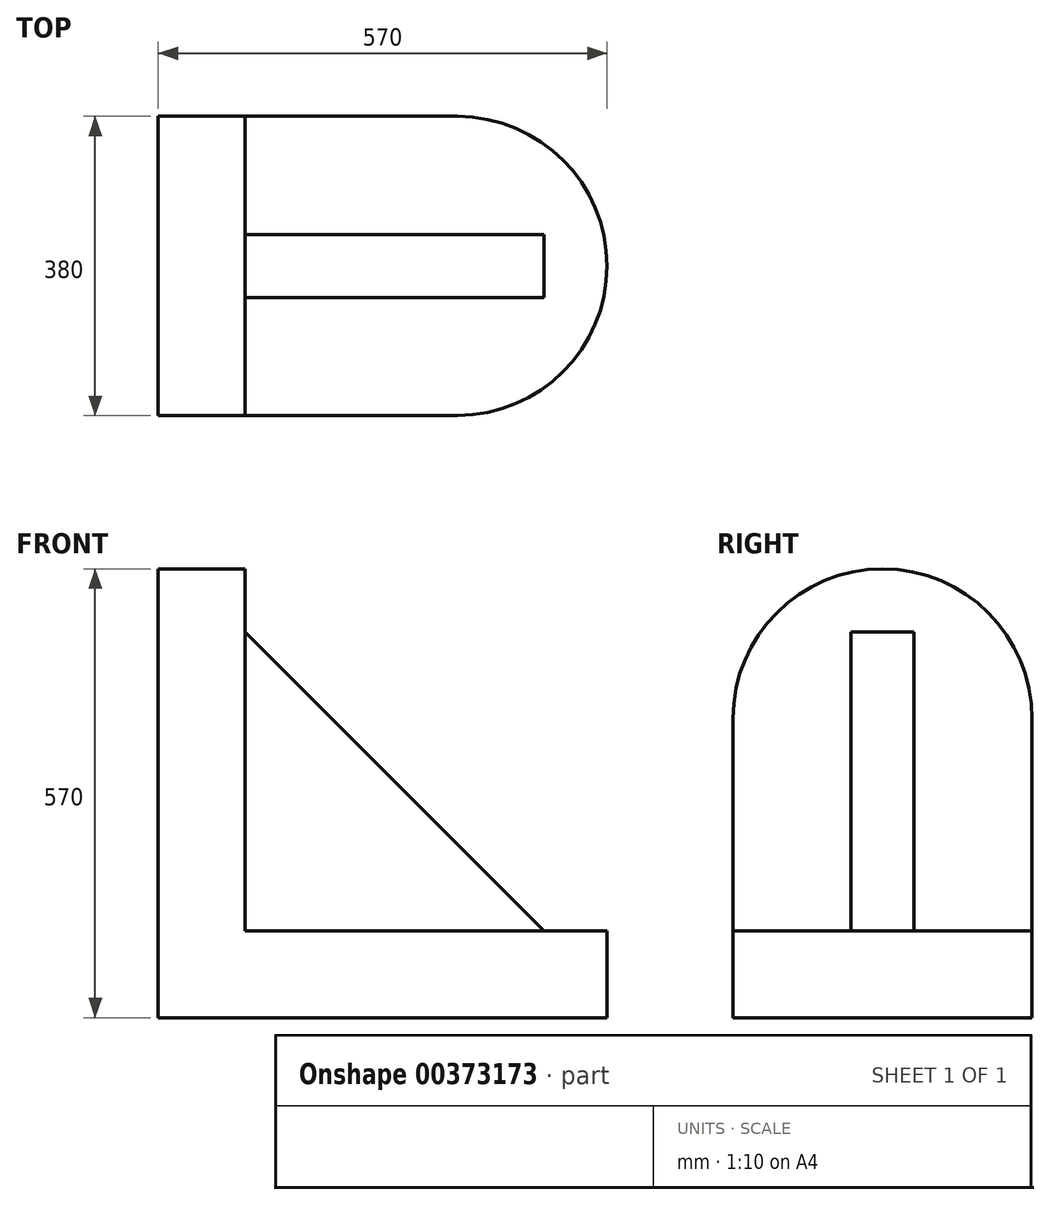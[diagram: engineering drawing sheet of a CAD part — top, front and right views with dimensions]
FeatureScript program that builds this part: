
annotation { "Feature Type Name" : "Feature", "Feature Type Description" : "" }
export const myFeature = defineFeature(function(context is Context, id is Id, definition is map)
    precondition{}
    {
        {
            var Q0;
            Q0=qCreatedBy(makeId("Top.planeOp"),FACE);
            var sketch = newSketch(context, id + "F0", { "sketchPlane" : qUnion([Q0])});
            skLineSegment(sketch, "E0.bottom", {"start": v(0, 0) * mm, "end": v(380, 0) * mm});
            skLineSegment(sketch, "E0.top", {"start": v(0, 380) * mm, "end": v(380, 380) * mm});
            skLineSegment(sketch, "E0.left", {"start": v(0, 0) * mm, "end": v(0, 380) * mm});
            skArc(sketch, "E1", {"start": v(380, 0) * mm, "mid": v(570, 190) * mm, "end": v(380, 380) * mm});
            skSolve(sketch);
        }
        {
            var Q0;
            Q0 = qSketchRegion(id + "F0", true);
            extrude(context, id + "F1", {"entities" : qUnion([Q0]), "depth" : 110 * mm});
        }
        {
            var Q0;
            Q0=makeQuery(id+"F1.opExtrude","CAP_FACE",FACE,{"disambiguationData":[OSD([sQuery(id+"F0.wireOp",EDGE,"E0.bottom"),sQuery(id+"F0.wireOp",EDGE,"E0.top"),sQuery(id+"F0.wireOp",EDGE,"E0.left"),sQuery(id+"F0.wireOp",EDGE,"E1")])],"isStart":false});
            var sketch = newSketch(context, id + "F2", { "sketchPlane" : qUnion([Q0])});
            skLineSegment(sketch, "E2.bottom", {"start": v(0, 380) * mm, "end": v(110, 380) * mm});
            skLineSegment(sketch, "E2.top", {"start": v(0, 0) * mm, "end": v(110, 0) * mm});
            skLineSegment(sketch, "E2.left", {"start": v(0, 380) * mm, "end": v(0, 0) * mm});
            skLineSegment(sketch, "E2.right", {"start": v(110, 380) * mm, "end": v(110, 0) * mm});
            skSolve(sketch);
        }
        {
            var Q0;
            Q0 = qSketchRegion(id + "F2", true);
            extrude(context, id + "F3", {"entities" : qUnion([Q0]), "operationType" : NewBodyOperationType.ADD, "depth" : 270 * mm + 190 * mm});
        }
        {
            var Q0;
            Q0=makeQuery(id+"F3.opExtrude","SWEPT_FACE",FACE,{"disambiguationData":[OSD([sQuery(id+"F2.wireOp",EDGE,"E2.right")])]});
            var sketch = newSketch(context, id + "F4", { "sketchPlane" : qUnion([Q0])});
            skLineSegment(sketch, "E3", {"start": v(0, 0) * mm, "end": v(0, 380) * mm});
            skArc(sketch, "E4", {"start": v(380, 380) * mm, "mid": v(190, 570) * mm, "end": v(0, 380) * mm});
            skSolve(sketch);
        }
        {
            var Q0;
            {var subQ0=sQuery(id+"F4.wireOp",EDGE,"E4");var subQ1=sQuery(id+"F2.wireOp",EDGE,"E2.right");var subQ4=makeQuery(id+"F3.opExtrude","CAP_EDGE",EDGE,{"disambiguationData":[OSD([subQ1])],"isStart":false});var subQ5=makeQuery(id+"F4.imprint","INTERSECT",VERTEX,{"derivedFrom":[subQ4,subQ0]});Q0=makeQuery(id+"F4.imprint","IMPRINT",FACE,{"disambiguationData":[TD([[makeQuery(id+"F4.imprint","IMPRINT",EDGE,{"disambiguationData":[TD([[subQ5,-1.0]])],"derivedFrom":subQ4}),1.0]])]});}
            var Q1;
            {var subQ0=sQuery(id+"F4.wireOp",EDGE,"E4");var subQ1=sQuery(id+"F2.wireOp",EDGE,"E2.right");var subQ4=makeQuery(id+"F3.opExtrude","CAP_EDGE",EDGE,{"disambiguationData":[OSD([subQ1])],"isStart":false});var subQ5=makeQuery(id+"F4.imprint","INTERSECT",VERTEX,{"derivedFrom":[subQ4,subQ0]});Q1=makeQuery(id+"F4.imprint","IMPRINT",FACE,{"disambiguationData":[TD([[makeQuery(id+"F4.imprint","IMPRINT",EDGE,{"disambiguationData":[TD([[subQ5,1.0]])],"derivedFrom":subQ0}),-1.0]])]});}
            extrude(context, id + "F5", {"entities" : qUnion([Q0, Q1]), "operationType" : NewBodyOperationType.REMOVE, "endBound" : BoundingType.THROUGH_ALL, "oppositeDirection" : true, "depth" : 25.4 * mm});
        }
        {
            var Q0;
            Q0=makeQuery(id+"F3.opExtrude","SWEPT_FACE",FACE,{"disambiguationData":[OSD([sQuery(id+"F2.wireOp",EDGE,"E2.right")])]});
            var sketch = newSketch(context, id + "F6", { "sketchPlane" : qUnion([Q0])});
            skLineSegment(sketch, "E5", {"start": v(190, 490) * mm, "end": v(150, 490) * mm});
            skLineSegment(sketch, "E6", {"start": v(150, 490) * mm, "end": v(150, 110) * mm});
            skLineSegment(sketch, "E7.MirrorCS", {"start": v(230, 490) * mm, "end": v(230, 110) * mm});
            skLineSegment(sketch, "E8.MirrorCS", {"start": v(190, 490) * mm, "end": v(230, 490) * mm});
            skPoint(sketch, "E9.start.orphan", {"position": v(190, 110) * mm});
            skSolve(sketch);
        }
        {
            var Q0;
            Q0=makeQuery(id+"F6.imprint","IMPRINT",FACE,{"disambiguationData":[TD([[makeQuery(id+"F6.imprint","IMPRINT",EDGE,{"derivedFrom":sQuery(id+"F6.wireOp",EDGE,"E5")}),1.0]])]});
            extrude(context, id + "F7", {"entities" : qUnion([Q0]), "operationType" : NewBodyOperationType.ADD, "depth" : 380 * mm});
        }
        {
            var Q0;
            Q0=makeQuery(id+"F7.opExtrude","SWEPT_FACE",FACE,{"disambiguationData":[OSD([sQuery(id+"F6.wireOp",EDGE,"E6")])]});
            var sketch = newSketch(context, id + "F8", { "sketchPlane" : qUnion([Q0])});
            skLineSegment(sketch, "E10", {"start": v(110, 490) * mm, "end": v(490, 110) * mm});
            skSolve(sketch);
        }
        {
            var Q0;
            Q0=makeQuery(id+"F8.imprint","IMPRINT",FACE,{"disambiguationData":[TD([[makeQuery(id+"F8.imprint","IMPRINT",EDGE,{"derivedFrom":sQuery(id+"F8.wireOp",EDGE,"E10")}),1.0]])]});
            extrude(context, id + "F9", {"entities" : qUnion([Q0]), "operationType" : NewBodyOperationType.REMOVE, "endBound" : BoundingType.THROUGH_ALL, "oppositeDirection" : true, "depth" : 25.4 * mm});
        }
    });
